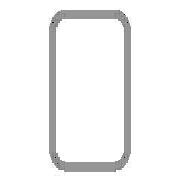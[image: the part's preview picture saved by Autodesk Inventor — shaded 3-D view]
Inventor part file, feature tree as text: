
AUTODESK INVENTOR PART (.ipt)
format: ipt  version: 2025 (Build 290162010, 162A)  size: 142,336 bytes
history: native  units: mm (DEFAULTED — no unit token found)
features: other x4, plane x2, split x1, sketch x1
ambient origin geometry x8: Origin, YZ Plane, XZ Plane, XY Plane, X Axis, Y Axis, Z Axis, Center Point
bodies: Solid1 (feature_tree), Body (feature_tree)
feature tree (8):
  parser-record x1  (decoder bookkeeping rows leaked as tree rows — omitted from the tree; the rows remain in map.json)
  other  "Driven Length"
  other  "Start Plane"
  other  "End Plane"
  plane  "Work Plane4"
  split  "Split1"
  sketch  "Sketch3"  dims[d3=809.237711mm d4=0.0mm d7=4.0mm d9=20.0mm d11=40.0mm d12=2.0mm d13=-0.0mm d14=809.237711mm d15=10.0mm d16=20.0mm d17=90.0deg d18=809.237711mm]
  plane  "Work Plane3"
